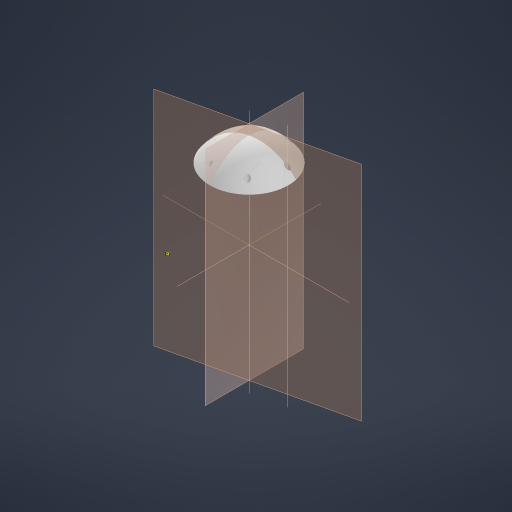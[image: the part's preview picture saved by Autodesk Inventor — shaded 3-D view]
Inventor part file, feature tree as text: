
AUTODESK INVENTOR PART (.ipt)
format: ipt  version: 2023 (Build 270158000, 158)  size: 2,373,120 bytes
history: native  units: mm
features: sketch x23, extrude x14, projected_geometry x12, other x10, reference x8, plane x6, pattern_circular x6, revolve x5, pattern_linear x2, sweep x1, chamfer x1, shell x1
ambient origin geometry x8: Origin, YZ Plane, XZ Plane, XY Plane, X Axis, Y Axis, Z Axis, Center Point
bodies: Solid1 (feature_tree)
feature tree (89):
  revolve  "Revolution1"  [1 undecoded]
  sketch  "3D Sketch1"
  plane  "Work Plane1"
  sweep  "Sweep1"
  pattern_circular  "Circular Pattern1"  Count=6 Angle=360.0deg
  extrude  "Extrusion1"  TaperAngle=0.0deg  [1 undecoded]
  revolve  "Revolution4"  [1 undecoded]
  extrude  "Extrusion10"  Depth=10.0mm
  revolve  "Revolution6"  [1 undecoded]
  pattern_circular  "Circular Pattern8"  Count=3 Angle=360.0deg
  extrude  "Extrusion17"  Depth=6.0mm
  plane  "Work Plane8"
  revolve  "Revolution7"  Angle=45.0deg
  pattern_circular  "Circular Pattern9"  Count=3 Angle=360.0deg
  extrude  "Extrusion12"  Depth=6.0mm
  extrude  "Extrusion13"  Depth=4.0mm TaperAngle=360.0deg
  extrude  "Extrusion14"  Depth=130.0mm
  extrude  "Extrusion15"  TaperAngle=90.0deg  [1 undecoded]
  extrude  "Extrusion16"  Depth=4.0mm
  pattern_linear  "Rectangular Pattern1"  Spacing1=26.0mm  [1 undecoded]
  pattern_linear  "Rectangular Pattern2"  Spacing1=66.5mm  [1 undecoded]
  plane  "Work Plane3"
  sketch  "Sketch12"  dims[d16=0.2mm]
  plane  "Work Plane6"
  extrude  "Extrusion6"  Depth=4.0mm TaperAngle=0.0deg
  chamfer  "Chamfer2"  Distance=25.9mm
  pattern_circular  "Circular Pattern4"  [2 undecoded]
  shell  "Shell2"  Thickness=1.6mm
  extrude  "Extrusion8"  Depth=4.0mm
  extrude  "Extrusion2"  Depth=4.0mm
  sketch  "Sketch7"  dims[d13=1.6mm]
  plane  "Work Plane4"
  extrude  "Extrusion3"  Depth=4.0mm TaperAngle=0.0deg
  extrude  "Extrusion4"  Depth=4.0mm TaperAngle=0.0deg
  pattern_circular  "Circular Pattern2"  [2 undecoded]
  extrude  "Extrusion7"  Depth=10.0mm TaperAngle=0.0deg
  pattern_circular  "Circular Pattern5"  Count=6  [1 undecoded]
  revolve  "Revolution2"  [1 undecoded]
  sketch  "Sketch1"  dims[d0=160.0mm d1=100.0mm]
  other  "Helical Curve2"
  other  "Project to Surface1"
  sketch  "Sketch2"  dims[d2=90.0deg d7=1200.0mm d8=637.649mm d9=252.623mm d10=0.0mm]
  sketch  "Sketch3"  dims[d11=15.0mm]
  plane  "Work Plane2"
  sketch  "Sketch6"  dims[d12=3.0mm]
  sketch  "Sketch8"  dims[d14=1.478932mm]
  sketch  "Sketch9"  dims[d15=0.2mm]
  sketch  "Sketch13"  dims[d17=0.2mm]
  sketch  "Sketch14"  dims[d18=0.0mm d19=0.0mm d20=60.0mm d21=360.0deg]
  reference  "Reference1"
  sketch  "Sketch15"  dims[d23=120.0mm d24=0.0mm d25=0.0mm]
  sketch  "Sketch16"  dims[d26=-130.0mm d27=-10.0mm d29=1.0mm]
  sketch  "Sketch18"  dims[d30=10.0mm d31=0.0mm d32=6.0mm]
  sketch  "Sketch21"  dims[d33=4.0mm d34=0.0mm d35=4.0mm]
  reference  "Reference10"
  sketch  "Sketch24"  dims[d36=4.0mm d37=0.0mm d38=30.0mm d39=360.0deg]
  projected_geometry  "Projected Loop3"
  sketch  "Sketch25"  dims[d51=100.0mm d52=6.0mm]
  projected_geometry  "Projected Loop4"
  sketch  "Sketch26"  dims[d53=4.0mm d54=0.0mm d55=3.5mm d56=1.0mm d57=45.0deg d58=30.0mm d59=360.0deg]
  projected_geometry  "Projected Loop5"
  sketch  "Sketch27"  dims[d61=30.0deg d62=6.0mm]
  sketch  "Sketch28"  dims[d63=4.0mm d64=0.0mm d65=60.0mm d66=360.0deg]
  sketch  "Sketch31"  dims[d68=360.0deg d69=130.0mm]
  sketch  "Sketch32"  dims[d70=0.0mm d71=0.0mm d73=90.0deg]
  reference  "Reference11"
  reference  "Reference12"
  reference  "Reference13"
  reference  "Reference14"
  reference  "Reference15"
  reference  "Reference16"
  other  "Work Axis2"
  sketch  "Sketch33"  dims[d83=5.0mm d84=3.3mm d85=26.0mm d86=0.0mm d89=66.5mm d90=150.0mm d91=0.0mm d92=25.9mm d93=1.6mm d94=0.0mm d95=1.6mm d96=1.6mm d97=1.6mm d98=30.0mm d99=0.0mm d100=30.0mm d101=0.0mm d102=4.0mm d103=10.0mm d104=0.0mm d105=60.0mm d107=10.0mm d108=70.0mm d110=10.0mm d111=100.0mm d113=10.0mm d114=60.0mm d116=10.0mm d117=1.3mm d118=1.3mm d124=1.2mm d125=6.457718mm d126=60.0mm d127=360.0deg d129=0.0mm d130=0.0mm d131=5.0mm d132=4.0mm d133=90.0deg d134=60.0mm d135=360.0deg]
  projected_geometry  "Projected Loop7"
  projected_geometry  "Project Cut Edges1"
  projected_geometry  "Project Cut Edges2"
  projected_geometry  "Project Cut Edges3"
  projected_geometry  "Project Cut Edges5"
  projected_geometry  "Project Cut Edges6"
  parser-record x2  (decoder bookkeeping rows leaked as tree rows — omitted from the tree; the rows remain in map.json)
  other  "Assembly1.iam"
  other  "lower_centering_ring:1"
  projected_geometry  "Project Cut Edges7"
  projected_geometry  "Project Cut Edges9"
  other  "top_centering_ring:1"
  projected_geometry  "Project Cut Edges10"
  other  "assembly.iam"
  other  "ring_oben:1"
note: 13 required parameter values undecoded (feature->parameter linkage not recoverable at this tier; creation-order binding heuristic only, values carry confidence <= 0.55)
note: 2 file-system paths scrubbed to <path> (originals preserved in map.json)